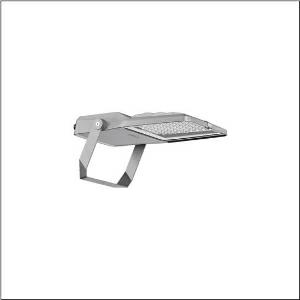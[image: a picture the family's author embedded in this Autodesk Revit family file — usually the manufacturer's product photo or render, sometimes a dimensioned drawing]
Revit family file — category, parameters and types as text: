
# Revit family: floodlight_fl_21_mini___pl61_5xa7775b2c1a_33c0
name_source: partatom
category: Lighting Fixtures
units: mm (PartAtom-declared; Revit-internal decimal feet)

## family parameters
Cut with Voids When Loaded = No
Host = Face
Light Source = No
Part Type = Normal
Room Calculation Point = No
Round Connector Dimension = Use Diameter
Shared = No

## types (1)
- --- (1 x LED, 6110 lm, 45.7 W, 3000K)
    Apparent Load = 46 VA
    CIE Flux Codes = 33 65 98 100 100
    Color Rendering = 70
    Color Temperature = 3000K
    Default Elevation = 1800 mm
    Description = Floodlight FL 21 mini, floodlight, primary light control with lens, of PMMA, primary optical cover: protective disc, of toughened safety glass, transparent, light distribution: PL61, light emission: direct distribution, installation type: surface-mounted, LED, High Power LED, rated luminous flux: 6.110lm, luminous efficacy: 134lm/W, light colour: 730, colour temperature: 3000K, control gear: ECG Smart Interface, control: flexible luminous flux parameterisation, time-dependent luminous flux control, constant luminous flux control, overheat protection, presetting dimming logarithmic, with terminal, 6-pole, mains connection: 220..240V, AC, 50/60Hz, start of lifetime: 46W, end of lifetime: 48W, reduction: 22W, luminaire housing, of diecast aluminium, powder-coated, Siteco® metallic grey (DB 702S), corrosivity category C5 according to DIN EN ISO 12944, mounting bracket, of steel, galvanised, powder-coated, Siteco® metallic grey (DB 702S), protection rating (complete): IP66, insulation class (complete): insulation class II (safety insulation), certification: CE, ENEC, VDE, protection symbol: D, impact resistance: IK08, permissible operating ambient temperature: -40..+40°C, permissible operating ambient temperature for outdoor applications: -40..+50°C, standard: DIN EN 12944, packaging unit: 1 piece

Light Distribution: PL61
    Height = 70 mm
    Lamp = 1 x LED
    Lamp Light Flux = 6110 lm
    Lamp Power = 45.7 W
    Lamp count = 1
    Length = 485 mm
    Luminous efficacy = 134 lm/W
    Manufacturer = Siteco
    ModVariant = No
    Model = 5XA7775B2C1A
    Number of Poles = 1
    OnlyDefault = Yes
    Power Factor = 1
    Product Name = Floodlight FL 21 mini | PL61
    Product group = floodlight | pylon top
    ProductGroupID = 6101
    Protection Class = Protection class II
    Protection Degree = IP 66
    RLX_Detail_Level = 1
    RlxData = <blob elided: 95953 chars, md5=76fc2669>
    Socket = socket
    Standby Power = 0 W
    System Light Flux = 6110 lm
    System Power = 46 W
    Type Comments = factory setting: luminous flux: 100 % | dim-lin: 254 | 463 mA
    Type Image = l_1006845.jpg
    URL = http://relux.com
    VarID = @adj_084553
    Voltage = 0 V
    Weight = 0.00 kg
    Width = 337 mm

## geometry (parser evidence)
native form markers: Blend x4, Sweep x10
no freeform markers — native parametric forms only
